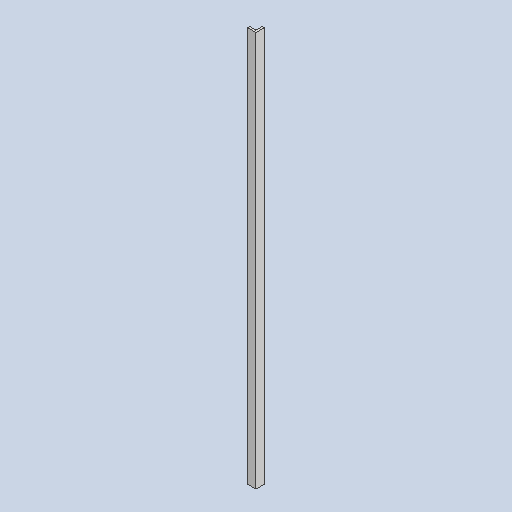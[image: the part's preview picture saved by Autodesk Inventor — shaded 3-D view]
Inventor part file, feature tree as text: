
AUTODESK INVENTOR PART (.ipt)
format: ipt  version: 2023 (Build 270158030, 158C)  size: 81,408 bytes
history: native  units: in
note: dims shown in document units (in); Inventor stores cm internally (conversion verified against a paired STEP export)
features: extrude x1, sketch x1
ambient origin geometry x8: Origin, YZ Plane, XZ Plane, XY Plane, X Axis, Y Axis, Z Axis, Center Point
bodies: Solid1 (feature_tree)
feature tree (2):
  extrude  "Extrusion1"  Depth=0.25in
  sketch  "Sketch1"  dims[d0=1.0in d1=0.25in d2=0.75in d3=0.75in d4=47.25in d5=0.0in]
